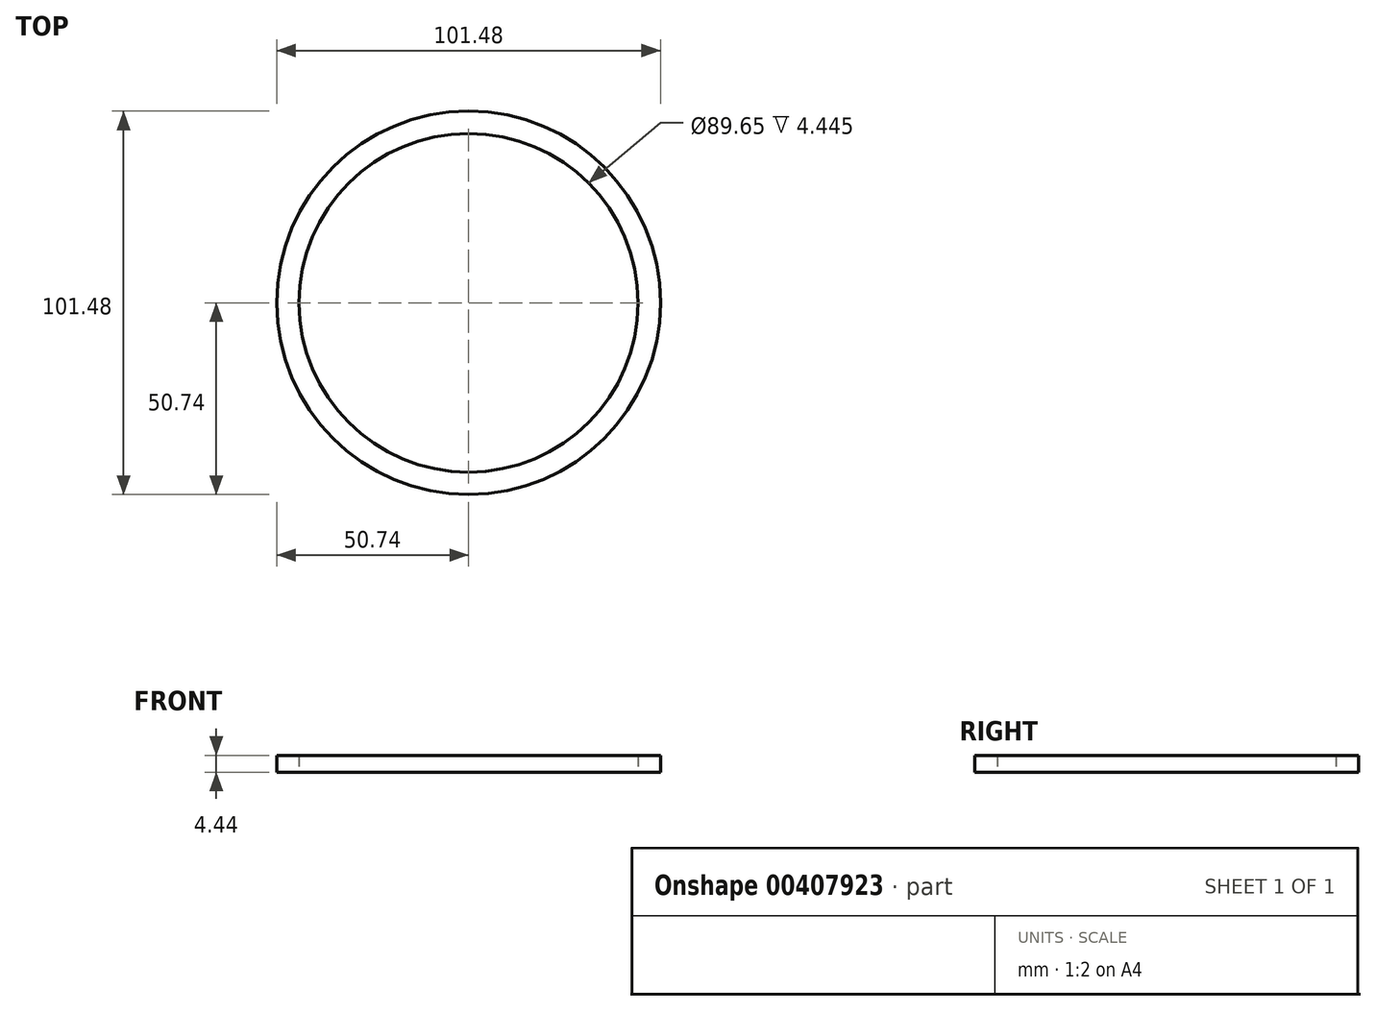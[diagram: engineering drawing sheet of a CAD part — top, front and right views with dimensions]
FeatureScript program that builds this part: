
annotation { "Feature Type Name" : "Feature", "Feature Type Description" : "" }
export const myFeature = defineFeature(function(context is Context, id is Id, definition is map)
    precondition{}
    {
        {
            var Q0;
            Q0=qCreatedBy(makeId("Top.planeOp"),FACE);
            var sketch = newSketch(context, id + "F0", { "sketchPlane" : qUnion([Q0])});
            skCircle(sketch, "E0", {"center": v(0, 0) * mm, "radius": 50.74 * mm});
            skCircle(sketch, "E1", {"center": v(0, 0) * mm, "radius": 44.82 * mm});
            skSolve(sketch);
        }
        {
            var Q0;
            Q0=makeQuery(id+"F0.imprint","IMPRINT",FACE,{"disambiguationData":[TD([[makeQuery(id+"F0.imprint","IMPRINT",EDGE,{"derivedFrom":sQuery(id+"F0.wireOp",EDGE,"E0")}),1.0]])]});
            extrude(context, id + "F1", {"entities" : qUnion([Q0]), "endBound" : BoundingType.SYMMETRIC, "depth" : 4.44 * mm});
        }
    });
